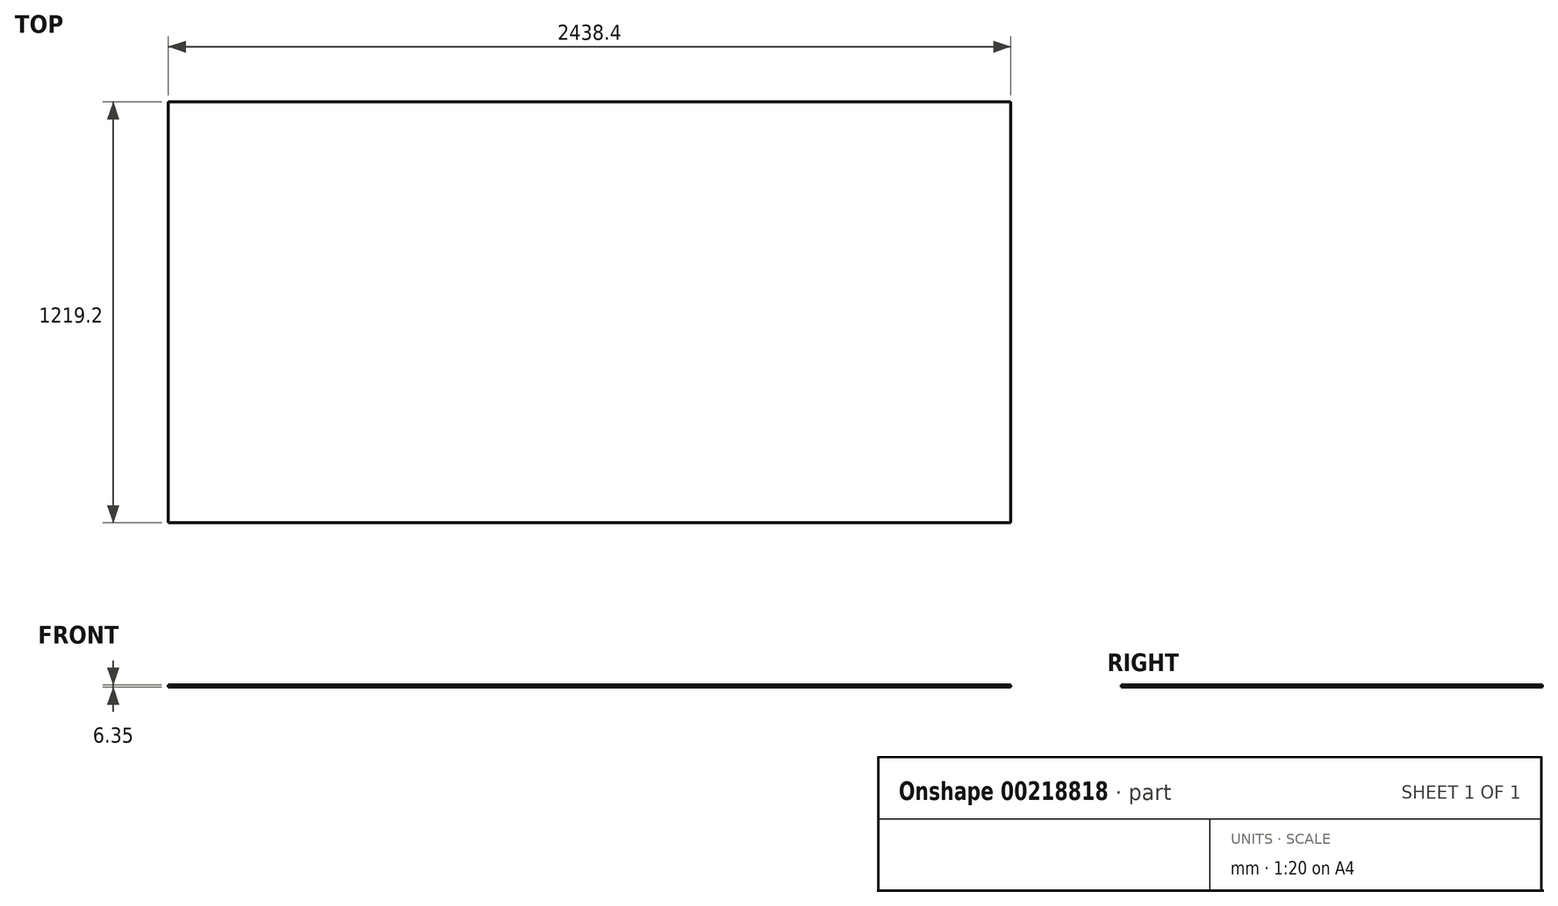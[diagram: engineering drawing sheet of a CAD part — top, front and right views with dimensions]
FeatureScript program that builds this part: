
annotation { "Feature Type Name" : "Feature", "Feature Type Description" : "" }
export const myFeature = defineFeature(function(context is Context, id is Id, definition is map)
    precondition{}
    {
        {
            var Q0;
            Q0=qCreatedBy(makeId("Top.planeOp"),FACE);
            var sketch = newSketch(context, id + "F0", { "sketchPlane" : qUnion([Q0])});
            skLineSegment(sketch, "E0.bottom", {"start": v(0, 0) * mm, "end": v(2438.4, 0) * mm});
            skLineSegment(sketch, "E0.top", {"start": v(0, -1219.2) * mm, "end": v(2438.4, -1219.2) * mm});
            skLineSegment(sketch, "E0.left", {"start": v(0, 0) * mm, "end": v(0, -1219.2) * mm});
            skLineSegment(sketch, "E0.right", {"start": v(2438.4, 0) * mm, "end": v(2438.4, -1219.2) * mm});
            skSolve(sketch);
        }
        {
            var Q0;
            Q0=makeQuery(id+"F0.imprint","IMPRINT",FACE,{"disambiguationData":[TD([[makeQuery(id+"F0.imprint","IMPRINT",EDGE,{"derivedFrom":sQuery(id+"F0.wireOp",EDGE,"E0.bottom")}),-1.0]])]});
            extrude(context, id + "F1", {"entities" : qUnion([Q0]), "depth" : 6.35 * mm});
        }
    });
